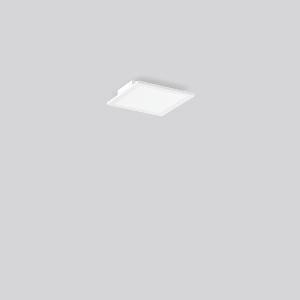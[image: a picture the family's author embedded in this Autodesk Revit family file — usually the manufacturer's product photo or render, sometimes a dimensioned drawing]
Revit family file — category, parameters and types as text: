
# Revit family: sidelite_eco_312375_002_7f18
name_source: partatom
category: Lighting Fixtures
units: mm (PartAtom-declared; Revit-internal decimal feet)

## family parameters
Cut with Voids When Loaded = No
Host = Face
Light Source = No
Part Type = Normal
Room Calculation Point = No
Round Connector Dimension = Use Diameter
Shared = No

## types (1)
- SIDELITE ECO (1 x LED Modul 830, 2100 lm, 3000)
    Apparent Load = 19 VA
    CIE Flux Codes = 47 79 96 100 100
    Color Rendering = 80
    Color Temperature = 3000
    Default Elevation = 1800 mm
    Description = Series: SIDELITE ECO
Highly economical surface mounted luminaire with progressive LED technology. Luminaire frame: aluminium, powder-coated. Mounting frame: sheet steel, powder-coated. Diffuser: plastic, opal. Lightguide and diffuser made of non-yellowing plastic (PMMA). Lateral light emission (RZB SIDELITE technology) for homogeneous light distribution. 
Colour: white
Length: 295 mm
Width: 295 mm
Height: 45.7 mm
Lamp: LED
Socket: without socket
Colour temperature: 3000K
Colour rendering index (CRI): 80
System power: 19 W
Rated luminous flux: 2100 lm
Luminous efficiency: 111 lm/W
Control gear: Regulated power supply
Protection class: II
Type of protection: IP 40
    Height = 46 mm
    Lamp = 1 x LED Modul 830
    Lamp Light Flux = 2100 lm
    Lamp count = 1
    Length = 295 mm
    Lifetime = 50000 h
    Luminous efficacy = 111 lm/W
    Manufacturer = RZB
    ModVariant = No
    Model = 312375.002
    Mounting Place = Ceiling
    Mounting Type = Surface mounted
    Number of Poles = 1
    OnlyDefault = Yes
    Power Factor = 1
    Product Name = SIDELITE ECO
    Product group = Surface mounted modular luminaires
    ProductGroupID = 306
    Protection Class = Protection class II
    Protection Degree = IP 40
    RLX_Detail_Level = 1
    RLX_Emergency_Light_Flux = 0 lm
    RLX_Emergency_Type = 0
    RLX_Emergency_Type_DB = No
    RlxData = <blob elided: 14241 chars, md5=daaf9157>
    Socket = socket
    Standby Power = 0 W
    System Light Flux = 2100 lm
    System Power = 19 W
    Type Comments = Product without accessories
    Type Image = 312375.002.jpg
    URL = http://relux.com
    VarID = ---
    Voltage = 230 V
    Voltage Range = 220-240 V
    Weight = 0.00 kg
    Width = 295 mm

## geometry (parser evidence)
native form markers: Sweep x12
no freeform markers — native parametric forms only
